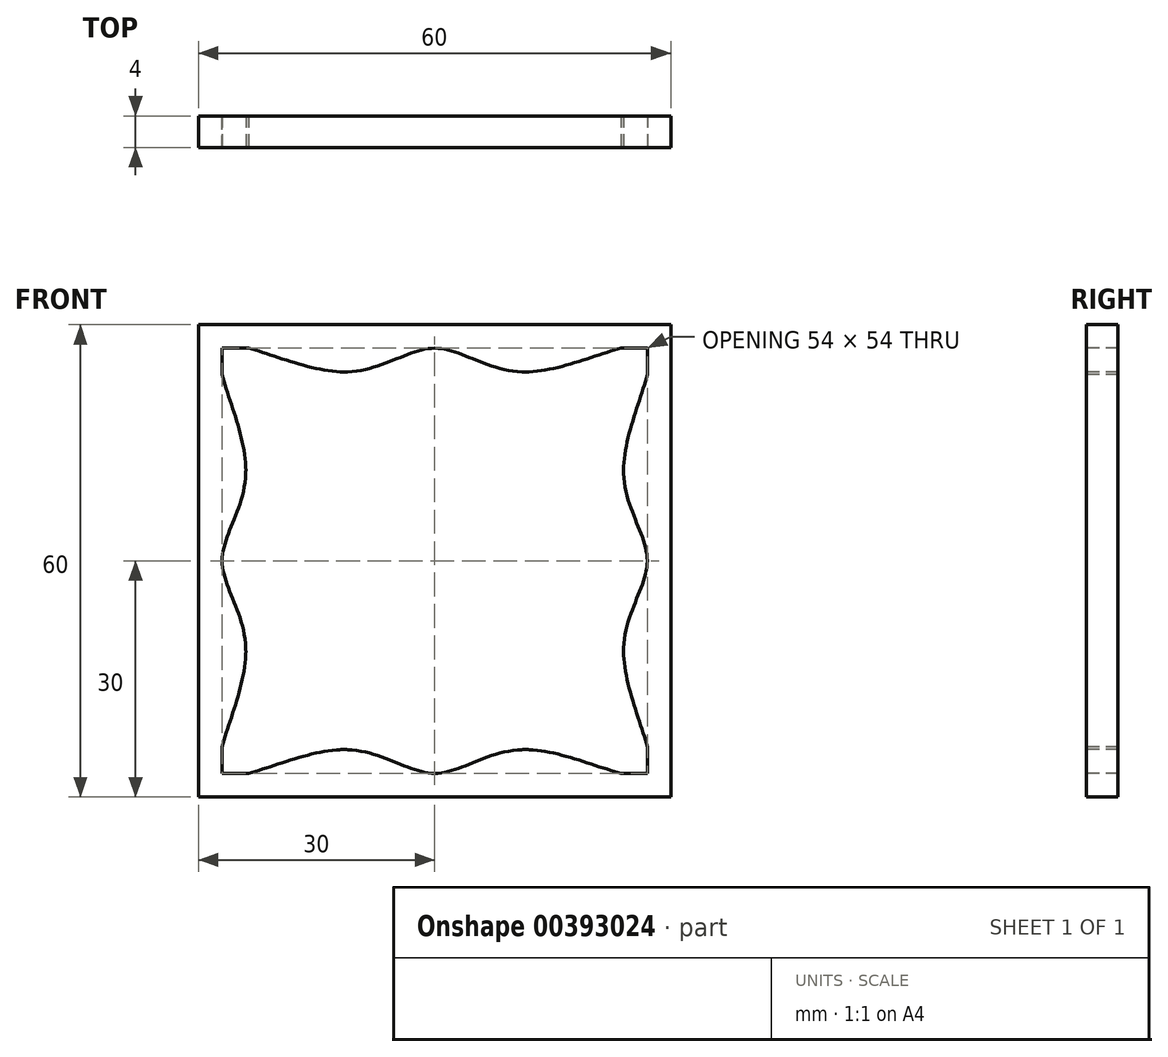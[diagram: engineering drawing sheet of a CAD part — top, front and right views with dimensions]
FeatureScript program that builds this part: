
annotation { "Feature Type Name" : "Feature", "Feature Type Description" : "" }
export const myFeature = defineFeature(function(context is Context, id is Id, definition is map)
    precondition{}
    {
        {
            var Q0;
            Q0=qCreatedBy(makeId("Front.planeOp"),FACE);
            var sketch = newSketch(context, id + "F0", { "sketchPlane" : qUnion([Q0])});
            skLineSegment(sketch, "E0.bottom", {"start": v(-30, 30) * mm, "end": v(30, 30) * mm});
            skLineSegment(sketch, "E0.top", {"start": v(-30, -30) * mm, "end": v(30, -30) * mm});
            skLineSegment(sketch, "E0.left", {"start": v(-30, 30) * mm, "end": v(-30, -30) * mm});
            skLineSegment(sketch, "E0.right", {"start": v(30, 30) * mm, "end": v(30, -30) * mm});
            skPoint(sketch, "E0.middle", {"position": v(0, 0) * mm});
            skSolve(sketch);
        }
        {
            var Q0;
            Q0 = qSketchRegion(id + "F0", true);
            extrude(context, id + "F1", {"entities" : qUnion([Q0]), "depth" : 4 * mm});
        }
        {
            var Q0;
            Q0=makeQuery(id+"F1.opExtrude","CAP_FACE",FACE,{"disambiguationData":[OSD([sQuery(id+"F0.wireOp",EDGE,"E0.bottom"),sQuery(id+"F0.wireOp",EDGE,"E0.top"),sQuery(id+"F0.wireOp",EDGE,"E0.left"),sQuery(id+"F0.wireOp",EDGE,"E0.right")])],"isStart":false});
            var sketch = newSketch(context, id + "F2", { "sketchPlane" : qUnion([Q0])});
            skLineSegment(sketch, "E1.0", {"start": v(-27, 27) * mm, "end": v(-27, -27) * mm});
            skLineSegment(sketch, "E1.1", {"start": v(27, 27) * mm, "end": v(-27, 27) * mm});
            skLineSegment(sketch, "E1.2", {"start": v(27, -27) * mm, "end": v(27, 27) * mm});
            skLineSegment(sketch, "E1.3", {"start": v(-27, -27) * mm, "end": v(27, -27) * mm});
            skLineSegment(sketch, "E2.0", {"start": v(-24, 24) * mm, "end": v(-24, 0) * mm});
            skLineSegment(sketch, "E2.1", {"start": v(24, 24) * mm, "end": v(0, 24) * mm});
            skLineSegment(sketch, "E2.2", {"start": v(24, -24) * mm, "end": v(24, 0) * mm});
            skLineSegment(sketch, "E2.3", {"start": v(-24, -24) * mm, "end": v(0, -24) * mm});
            skLineSegment(sketch, "E3", {"start": v(0, 27) * mm, "end": v(0, -27) * mm, "construction": true});
            skLineSegment(sketch, "E4", {"start": v(27, 0) * mm, "end": v(-27, 0) * mm, "construction": true});
            skLineSegment(sketch, "E5", {"start": v(-24, 0) * mm, "end": v(-24, -24) * mm});
            skLineSegment(sketch, "E6", {"start": v(24, 0) * mm, "end": v(24, 24) * mm});
            skLineSegment(sketch, "E7", {"start": v(0, 24) * mm, "end": v(-24, 24) * mm});
            skLineSegment(sketch, "E8", {"start": v(0, -24) * mm, "end": v(24, -24) * mm});
            skLineSegment(sketch, "E9", {"start": v(-12, 27) * mm, "end": v(-12, -27) * mm, "construction": true});
            skPoint(sketch, "E9.startSnap0", {"position": v(-12, 24) * mm});
            skPoint(sketch, "E9.endSnap0", {"position": v(-12, -24) * mm});
            skLineSegment(sketch, "E10", {"start": v(12, 27) * mm, "end": v(12, -27) * mm, "construction": true});
            skPoint(sketch, "E10.startSnap0", {"position": v(12, 24) * mm});
            skPoint(sketch, "E10.endSnap0", {"position": v(12, -24) * mm});
            skLineSegment(sketch, "E11", {"start": v(27, 12) * mm, "end": v(-27, 12) * mm, "construction": true});
            skPoint(sketch, "E11.startSnap0", {"position": v(24, 12) * mm});
            skLineSegment(sketch, "E12", {"start": v(27, -12) * mm, "end": v(-27, -12) * mm, "construction": true});
            skPoint(sketch, "E12.startSnap0", {"position": v(24, -12) * mm});
            skFitSpline(sketch, "E13", {"points": [v(-27, 27) * mm, v(-12, 24) * mm, v(0, 27) * mm, v(12, 24) * mm, v(27, 27) * mm, v(24, 12) * mm, v(27, 0) * mm, v(24, -12) * mm, v(27, -27) * mm, v(12, -24) * mm, v(0, -27) * mm, v(-12, -24) * mm, v(-27, -27) * mm, v(-24, -12) * mm, v(-27, 0) * mm, v(-24, 12) * mm, v(-27, 27) * mm]});
            skSolve(sketch);
        }
        {
            var Q0;
            {var subQ8=sQuery(id+"F2.wireOp",EDGE,"E7");var subQ9=sQuery(id+"F2.wireOp",EDGE,"E2.0");var subQ10=makeQuery(id+"F2.imprint","INTERSECT",VERTEX,{"derivedFrom":[subQ9,subQ8]});Q0=makeQuery(id+"F2.imprint","IMPRINT",FACE,{"disambiguationData":[TD([[makeQuery(id+"F2.imprint","IMPRINT",EDGE,{"disambiguationData":[TD([[subQ10,-1.0]])],"derivedFrom":subQ9}),1.0]])]});}
            var Q1;
            {var subQ0=sQuery(id+"F2.wireOp",EDGE,"E7");var subQ1=sQuery(id+"F2.wireOp",EDGE,"E2.0");var subQ2=makeQuery(id+"F2.imprint","INTERSECT",VERTEX,{"derivedFrom":[subQ1,subQ0]});Q1=makeQuery(id+"F2.imprint","IMPRINT",FACE,{"disambiguationData":[TD([[makeQuery(id+"F2.imprint","IMPRINT",EDGE,{"disambiguationData":[TD([[subQ2,-1.0]])],"derivedFrom":subQ1}),-1.0]])]});}
            var Q2;
            {var subQ0=sQuery(id+"F2.wireOp",EDGE,"E7");var subQ1=sQuery(id+"F2.wireOp",EDGE,"E2.1");var subQ2=makeQuery(id+"F2.imprint","INTERSECT",VERTEX,{"derivedFrom":[subQ1,subQ0]});Q2=makeQuery(id+"F2.imprint","IMPRINT",FACE,{"disambiguationData":[TD([[makeQuery(id+"F2.imprint","IMPRINT",EDGE,{"disambiguationData":[TD([[subQ2,1.0]])],"derivedFrom":subQ1}),-1.0]])]});}
            var Q3;
            {var subQ0=sQuery(id+"F2.wireOp",EDGE,"E6");var subQ1=sQuery(id+"F2.wireOp",EDGE,"E2.1");var subQ2=makeQuery(id+"F2.imprint","INTERSECT",VERTEX,{"derivedFrom":[subQ1,subQ0]});Q3=makeQuery(id+"F2.imprint","IMPRINT",FACE,{"disambiguationData":[TD([[makeQuery(id+"F2.imprint","IMPRINT",EDGE,{"disambiguationData":[TD([[subQ2,-1.0]])],"derivedFrom":subQ1}),-1.0]])]});}
            var Q4;
            {var subQ0=sQuery(id+"F2.wireOp",EDGE,"E6");var subQ1=sQuery(id+"F2.wireOp",EDGE,"E2.2");var subQ2=makeQuery(id+"F2.imprint","INTERSECT",VERTEX,{"derivedFrom":[subQ1,subQ0]});Q4=makeQuery(id+"F2.imprint","IMPRINT",FACE,{"disambiguationData":[TD([[makeQuery(id+"F2.imprint","IMPRINT",EDGE,{"disambiguationData":[TD([[subQ2,1.0]])],"derivedFrom":subQ1}),-1.0]])]});}
            var Q5;
            {var subQ0=sQuery(id+"F2.wireOp",EDGE,"E8");var subQ1=sQuery(id+"F2.wireOp",EDGE,"E2.2");var subQ2=makeQuery(id+"F2.imprint","INTERSECT",VERTEX,{"derivedFrom":[subQ1,subQ0]});Q5=makeQuery(id+"F2.imprint","IMPRINT",FACE,{"disambiguationData":[TD([[makeQuery(id+"F2.imprint","IMPRINT",EDGE,{"disambiguationData":[TD([[subQ2,-1.0]])],"derivedFrom":subQ1}),-1.0]])]});}
            var Q6;
            {var subQ0=sQuery(id+"F2.wireOp",EDGE,"E8");var subQ1=sQuery(id+"F2.wireOp",EDGE,"E2.3");var subQ2=makeQuery(id+"F2.imprint","INTERSECT",VERTEX,{"derivedFrom":[subQ1,subQ0]});Q6=makeQuery(id+"F2.imprint","IMPRINT",FACE,{"disambiguationData":[TD([[makeQuery(id+"F2.imprint","IMPRINT",EDGE,{"disambiguationData":[TD([[subQ2,1.0]])],"derivedFrom":subQ1}),-1.0]])]});}
            var Q7;
            {var subQ0=sQuery(id+"F2.wireOp",EDGE,"E5");var subQ1=sQuery(id+"F2.wireOp",EDGE,"E2.3");var subQ2=makeQuery(id+"F2.imprint","INTERSECT",VERTEX,{"derivedFrom":[subQ1,subQ0]});Q7=makeQuery(id+"F2.imprint","IMPRINT",FACE,{"disambiguationData":[TD([[makeQuery(id+"F2.imprint","IMPRINT",EDGE,{"disambiguationData":[TD([[subQ2,-1.0]])],"derivedFrom":subQ1}),-1.0]])]});}
            var Q8;
            {var subQ0=sQuery(id+"F2.wireOp",EDGE,"E5");var subQ1=sQuery(id+"F2.wireOp",EDGE,"E2.0");var subQ2=makeQuery(id+"F2.imprint","INTERSECT",VERTEX,{"derivedFrom":[subQ1,subQ0]});Q8=makeQuery(id+"F2.imprint","IMPRINT",FACE,{"disambiguationData":[TD([[makeQuery(id+"F2.imprint","IMPRINT",EDGE,{"disambiguationData":[TD([[subQ2,1.0]])],"derivedFrom":subQ1}),-1.0]])]});}
            extrude(context, id + "F3", {"entities" : qUnion([Q0, Q1, Q2, Q3, Q4, Q5, Q6, Q7, Q8]), "operationType" : NewBodyOperationType.REMOVE, "oppositeDirection" : true, "depth" : 4 * mm});
        }
    });
